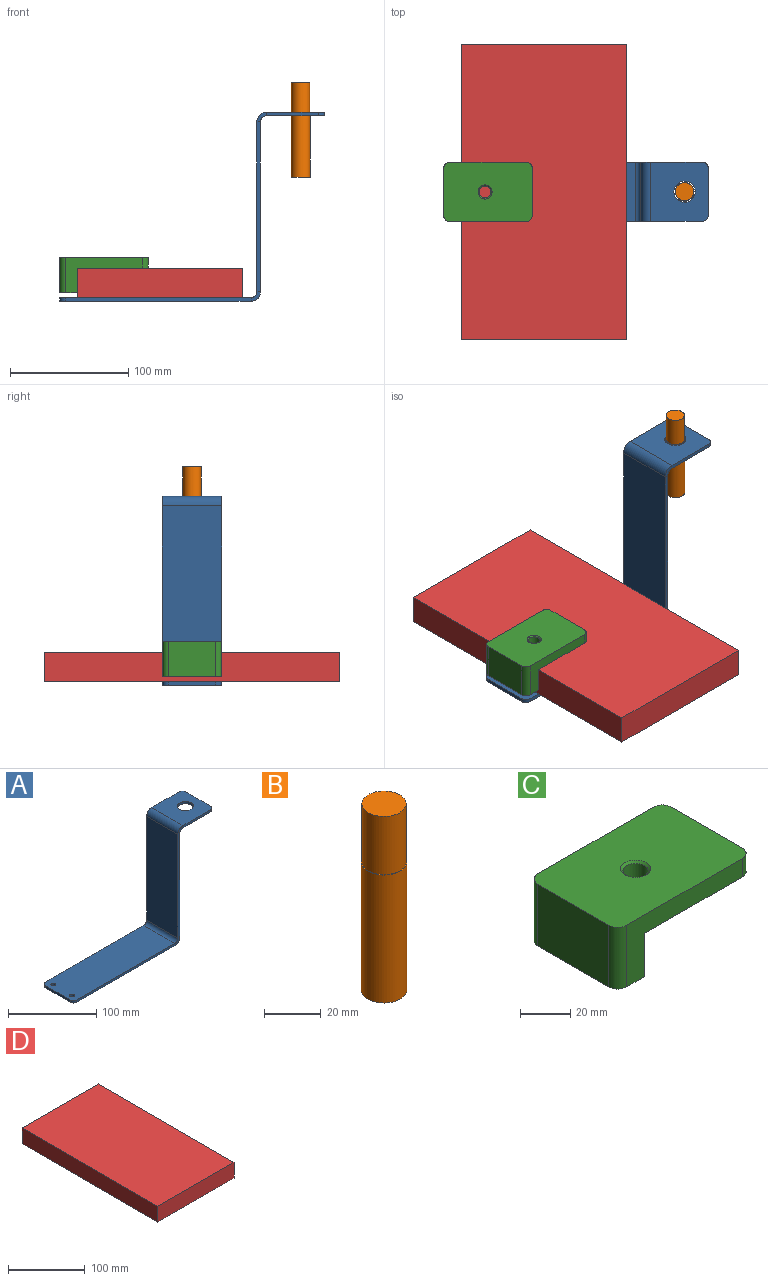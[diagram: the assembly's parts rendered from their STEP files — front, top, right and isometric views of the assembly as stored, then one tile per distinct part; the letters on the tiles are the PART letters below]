
ASSEMBLY  parts=4 mates=3
PART A: 29 faces, bbox 224x50x160 mm
  f0: plane 44x3mm, normal (0,1,0), area 132mm2, adj f4,f5,f7,f26
  f1: plane 44x3mm, normal (0,-1,0), area 132mm2, adj f4,f5,f6,f25
  f2: cylinder r=9mm len=18mm, axis (0,0,1), area 169.6mm2, adj f4,f5
  f3: plane 40x3mm, normal (1,0,0), area 120mm2, adj f4,f5,f6,f7
  f4: plane 50x49mm, normal (0,0,1), area 2184.8mm2, adj f0,f1,f2,f3,f6,f7,f27
  f5: plane 50x49mm, normal (0,0,-1), area 2184.8mm2, adj f0,f1,f2,f3,f6,f7,f28
  f6: cylinder r=5mm len=5mm, axis (0,0,1), area 23.6mm2, adj f1,f3,f4,f5
  f7: cylinder r=5mm len=5mm, axis (0,0,-1), area 23.6mm2, adj f0,f3,f4,f5
  f8: plane 144x3mm, normal (0,1,0), area 432mm2, adj f10,f11,f22,f26
  f9: plane 144x3mm, normal (0,-1,0), area 432mm2, adj f10,f11,f21,f25
  f10: plane 144x50mm, normal (-1,0,0), area 7200mm2, adj f8,f9,f24,f27
  f11: plane 144x50mm, normal (1,0,0), area 7200mm2, adj f8,f9,f23,f28
  f12: plane 157x3mm, normal (0,1,0), area 471mm2, adj f17,f18,f19,f22
  f13: plane 40x3mm, normal (-1,0,0), area 120mm2, adj f17,f18,f19,f20
  f14: plane 157x3mm, normal (0,-1,0), area 471mm2, adj f17,f18,f20,f21
  f15: cylinder r=2.75mm len=5.5mm, axis (0,0,1), area 51.8mm2, adj f17,f18
  f16: cylinder r=2.75mm len=5.5mm, axis (0,0,1), area 51.8mm2, adj f17,f18
  f17: plane 162x50mm, normal (0,0,1), area 8041.8mm2, adj f12,f13,f14,f15,f16,f19,f20,f24
  f18: plane 162x50mm, normal (0,0,-1), area 8041.8mm2, adj f12,f13,f14,f15,f16,f19,f20,f23
  f19: cylinder r=5mm len=5mm, axis (0,0,1), area 23.6mm2, adj f12,f13,f17,f18
  f20: cylinder r=5mm len=5mm, axis (0,0,-1), area 23.6mm2, adj f13,f14,f17,f18
  f21: plane 8x8mm, normal (0,-1,0), area 30.6mm2, adj f9,f14,f23,f24
  f22: plane 8x8mm, normal (0,1,0), area 30.6mm2, adj f8,f12,f23,f24
  f23: cylinder r=8mm len=50mm, axis (0,-1,0), area 628.3mm2, adj f11,f18,f21,f22
  f24: cylinder r=5mm len=50mm, axis (0,-1,0), area 392.7mm2, adj f10,f17,f21,f22
  f25: plane 8x8mm, normal (0,-1,0), area 30.6mm2, adj f1,f9,f27,f28
  f26: plane 8x8mm, normal (0,1,0), area 30.6mm2, adj f0,f8,f27,f28
  f27: cylinder r=8mm len=50mm, axis (0,-1,0), area 628.3mm2, adj f4,f10,f25,f26
  f28: cylinder r=5mm len=50mm, axis (0,-1,0), area 392.7mm2, adj f5,f11,f25,f26
PART B: 5 faces, bbox 16x16x80 mm
  f0: cylinder r=8mm len=55mm, axis (0,0,-1), area 2764.6mm2, adj f1,f2
  f1: plane 16x16mm, normal (0,0,-1), area 201.1mm2, adj f0
  f2: plane 16x16mm, normal (0,0,1), area 12.4mm2, adj f0,f3
  f3: cylinder r=7.75mm len=25mm, axis (0,0,1), area 1217.4mm2, adj f2,f4
  f4: plane 15.5x15.5mm, normal (0,0,1), area 188.7mm2, adj f3
PART C: 21 faces, bbox 75x50x30 mm
  f0: plane 40x9mm, normal (1,0,0), area 360mm2, adj f4,f6,f8,f9
  f1: plane 65x30mm, normal (0,-1,0), area 795mm2, adj f4,f5,f6,f7,f8,f11
  f2: plane 65x30mm, normal (0,1,0), area 795mm2, adj f4,f5,f6,f7,f9,f10
  f3: plane 40x30mm, normal (-1,0,0), area 1200mm2, adj f4,f5,f10,f11
  f4: plane 75x50mm, normal (0,0,1), area 3615.4mm2, adj f0,f1,f2,f3,f8,f9,f10,f11
  f5: plane 50x15mm, normal (0,0,-1), area 662.3mm2, adj f1,f2,f3,f7,f10,f11,f17,f18
  f6: plane 60x50mm, normal (0,0,-1), area 2876.2mm2, adj f0,f1,f2,f7,f8,f9,f19
  f7: plane 50x21mm, normal (1,0,0), area 1050mm2, adj f1,f2,f5,f6
  f8: cylinder r=5mm len=9mm, axis (0,0,1), area 70.7mm2, adj f0,f1,f4,f6
  f9: cylinder r=5mm len=9mm, axis (0,0,-1), area 70.7mm2, adj f0,f2,f4,f6
  f10: cylinder r=5mm len=30mm, axis (0,0,1), area 235.6mm2, adj f2,f3,f4,f5
  f11: cylinder r=5mm len=30mm, axis (0,0,-1), area 235.6mm2, adj f1,f3,f4,f5
  f12: cylinder r=5mm len=10mm, axis (0,0,1), area 219.9mm2, adj f19,f20
  f13: cylinder r=2.5mm len=11mm, axis (0,0,-1), area 172.8mm2, adj f14,f17
  f14: plane 5x5mm, normal (0,0,-1), area 19.6mm2, adj f13
  f15: cylinder r=2.5mm len=11mm, axis (0,0,-1), area 172.8mm2, adj f16,f18
  f16: plane 5x5mm, normal (0,0,-1), area 19.6mm2, adj f15
  f17: cone r=2.5mm half-angle=45deg, axis (0,0,-1), area 26.7mm2, adj f5,f13
  f18: cone r=2.5mm half-angle=45deg, axis (0,0,-1), area 26.7mm2, adj f5,f15
  f19: cone r=6mm half-angle=45deg, axis (0,0,-1), area 48.9mm2, adj f6,f12
  f20: cone r=5mm half-angle=45deg, axis (0,0,1), area 48.9mm2, adj f4,f12
PART D: 6 faces, bbox 140x250x25 mm
  f0: plane 140x25mm, normal (0,-1,0), area 3500mm2, adj f1,f3,f4,f5
  f1: plane 250x25mm, normal (1,0,0), area 6250mm2, adj f0,f2,f4,f5
  f2: plane 140x25mm, normal (0,1,0), area 3500mm2, adj f1,f3,f4,f5
  f3: plane 250x25mm, normal (-1,0,0), area 6250mm2, adj f0,f2,f4,f5
  f4: plane 250x140mm, normal (0,0,1), area 35000mm2, adj f0,f1,f2,f3
  f5: plane 250x140mm, normal (0,0,-1), area 35000mm2, adj f0,f1,f2,f3
PLACE A t=(184.25,0,-37.82)mm
PLACE B t=(569.69,0,-89.82)mm
PLACE C t=(235.87,0,-187.82)mm
PLACE D t=(283.37,265.04,-191.82)mm fixed
MATE fastened B.f0 <-> A.f2  axis (0,0,1) through (402.37,0,-34.82)mm
MATE fastened C.f6 <-> D.f4  axis (0,0,-1) through (213.37,0,-166.82)mm
MATE fastened A.f15 <-> C.f15  axis (0,0,1) through (205.87,-15,-191.82)mm
